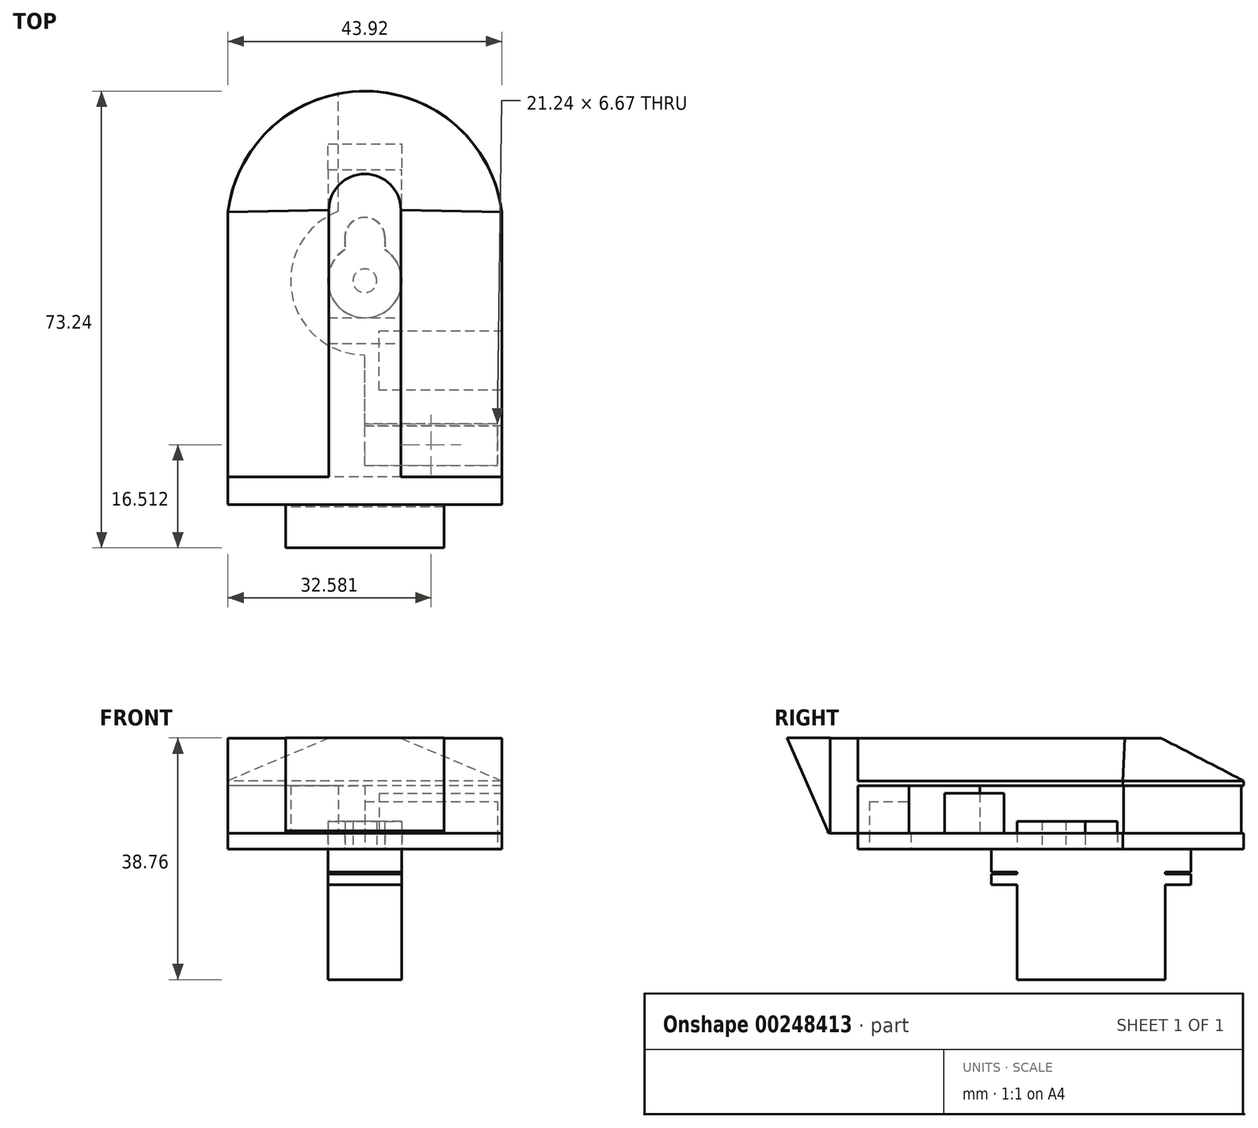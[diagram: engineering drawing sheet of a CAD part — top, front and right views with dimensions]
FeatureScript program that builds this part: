
annotation { "Feature Type Name" : "Feature", "Feature Type Description" : "" }
export const myFeature = defineFeature(function(context is Context, id is Id, definition is map)
    precondition{}
    {
        {
            var Q0;
            Q0=qCreatedBy(makeId("Top.planeOp"),FACE);
            var sketch = newSketch(context, id + "F0", { "sketchPlane" : qUnion([Q0])});
            skLineSegment(sketch, "E0", {"start": v(-5.9, 11.87) * mm, "end": v(-5.9, -11.87) * mm});
            skLineSegment(sketch, "E1", {"start": v(-5.9, -11.87) * mm, "end": v(5.9, -11.87) * mm});
            skLineSegment(sketch, "E2", {"start": v(5.9, -11.87) * mm, "end": v(5.9, 11.87) * mm});
            skLineSegment(sketch, "E3", {"start": v(5.9, 11.87) * mm, "end": v(-5.9, 11.87) * mm});
            skLineSegment(sketch, "E4", {"start": v(-5.9, 11.87) * mm, "end": v(-5.9, 16) * mm});
            skLineSegment(sketch, "E5", {"start": v(-5.9, 16) * mm, "end": v(5.9, 16) * mm});
            skLineSegment(sketch, "E6", {"start": v(5.9, 16) * mm, "end": v(5.9, 11.87) * mm});
            skLineSegment(sketch, "E7.MirrorCS", {"start": v(-5.9, -11.87) * mm, "end": v(-5.9, -16) * mm});
            skLineSegment(sketch, "E8.MirrorCS", {"start": v(-5.9, -16) * mm, "end": v(5.9, -16) * mm});
            skLineSegment(sketch, "E9.MirrorCS", {"start": v(5.9, -16) * mm, "end": v(5.9, -11.87) * mm});
            skSolve(sketch);
        }
        {
            var Q0;
            Q0=makeQuery(id+"F0.imprint","IMPRINT",FACE,{"disambiguationData":[TD([[makeQuery(id+"F0.imprint","IMPRINT",EDGE,{"derivedFrom":sQuery(id+"F0.wireOp",EDGE,"E0")}),1.0]])]});
            extrude(context, id + "F1", {"entities" : qUnion([Q0]), "oppositeDirection" : true, "depth" : 15.24 * mm});
        }
        {
            var Q0;
            Q0=makeQuery(id+"F0.imprint","IMPRINT",FACE,{"disambiguationData":[TD([[makeQuery(id+"F0.imprint","IMPRINT",EDGE,{"derivedFrom":sQuery(id+"F0.wireOp",EDGE,"E0")}),1.0]])]});
            extrude(context, id + "F2", {"entities" : qUnion([Q0]), "operationType" : NewBodyOperationType.ADD, "depth" : 5.7 * mm});
        }
        {
            var Q0;
            Q0=makeQuery(id+"F2.opExtrude","CAP_FACE",FACE,{"disambiguationData":[OSD([sQuery(id+"F0.wireOp",EDGE,"E0"),sQuery(id+"F0.wireOp",EDGE,"E1"),sQuery(id+"F0.wireOp",EDGE,"E2"),sQuery(id+"F0.wireOp",EDGE,"E3")])],"isStart":false});
            var sketch = newSketch(context, id + "F3", { "sketchPlane" : qUnion([Q0])});
            skArc(sketch, "E10", {"start": v(-3.17, -0.96) * mm, "mid": v(0, -11.85) * mm, "end": v(3.17, -0.96) * mm});
            skCircle(sketch, "E11", {"center": v(0, -5.94) * mm, "radius": 1.9 * mm});
            skArc(sketch, "E12", {"start": v(3.17, 1.02) * mm, "mid": v(0, 4.2) * mm, "end": v(-3.17, 1.02) * mm});
            skLineSegment(sketch, "E13", {"start": v(-3.17, 1.02) * mm, "end": v(-3.17, -0.96) * mm});
            skLineSegment(sketch, "E14", {"start": v(3.17, 1.02) * mm, "end": v(3.17, -0.96) * mm});
            skSolve(sketch);
        }
        {
            var Q0;
            Q0 = qSketchRegion(id + "F3", true);
            extrude(context, id + "F4", {"entities" : qUnion([Q0]), "operationType" : NewBodyOperationType.ADD, "depth" : 4.44 * mm});
        }
        {
            var Q0;
            Q0=makeQuery(id+"F0.imprint","IMPRINT",FACE,{"disambiguationData":[TD([[makeQuery(id+"F0.imprint","IMPRINT",EDGE,{"derivedFrom":sQuery(id+"F0.wireOp",EDGE,"E1")}),-1.0]])]});
            var Q1;
            Q1=makeQuery(id+"F0.imprint","IMPRINT",FACE,{"disambiguationData":[TD([[makeQuery(id+"F0.imprint","IMPRINT",EDGE,{"derivedFrom":sQuery(id+"F0.wireOp",EDGE,"E3")}),-1.0]])]});
            extrude(context, id + "F5", {"entities" : qUnion([Q0, Q1]), "operationType" : NewBodyOperationType.ADD, "depth" : 1.68 * mm});
        }
        {
            var Q0;
            Q0=qCreatedBy(makeId("Top.planeOp"),FACE);
            cPlane(context, id + "F6", {"entities" : qUnion([Q0]), "cplaneType" : CPlaneType.OFFSET, "offset" : 5.7 * mm, "width" : 152.4 * mm, "height" : 152.4 * mm});
        }
        {
            var Q0;
            Q0=qCreatedBy(id+"F6.planeOp",FACE);
            var sketch = newSketch(context, id + "F7", { "sketchPlane" : qUnion([Q0])});
            skLineSegment(sketch, "E15", {"start": v(21.96, -37.36) * mm, "end": v(-21.96, -37.36) * mm});
            skLineSegment(sketch, "E16", {"start": v(-21.96, -37.36) * mm, "end": v(-21.96, 5.1) * mm});
            skLineSegment(sketch, "E17", {"start": v(21.96, -37.36) * mm, "end": v(21.96, 5.1) * mm});
            skArc(sketch, "E18", {"start": v(21.96, 5.1) * mm, "mid": v(0, 24.49) * mm, "end": v(-21.96, 5.1) * mm});
            skArc(sketch, "E19", {"start": v(-3.23, -0.92) * mm, "mid": v(0, -11.87) * mm, "end": v(3.23, -0.92) * mm});
            skArc(sketch, "E20", {"start": v(3.23, 1.01) * mm, "mid": v(0, 4.25) * mm, "end": v(-3.23, 1.01) * mm});
            skLineSegment(sketch, "E21", {"start": v(-3.23, 1.01) * mm, "end": v(-3.23, -0.92) * mm});
            skLineSegment(sketch, "E22", {"start": v(3.23, 1.01) * mm, "end": v(3.23, -0.92) * mm});
            skSolve(sketch);
        }
        {
            var Q0;
            Q0 = qSketchRegion(id + "F7", true);
            extrude(context, id + "F8", {"entities" : qUnion([Q0]), "depth" : 2.54 * mm});
        }
        {
            var Q0;
            Q0=makeQuery(id+"F8.opExtrude","CAP_FACE",FACE,{"disambiguationData":[OSD([sQuery(id+"F7.wireOp",EDGE,"E15"),sQuery(id+"F7.wireOp",EDGE,"E16"),sQuery(id+"F7.wireOp",EDGE,"E17"),sQuery(id+"F7.wireOp",EDGE,"E18"),sQuery(id+"F7.wireOp",EDGE,"E19"),sQuery(id+"F7.wireOp",EDGE,"E20"),sQuery(id+"F7.wireOp",EDGE,"E21"),sQuery(id+"F7.wireOp",EDGE,"E22")])],"isStart":false});
            var sketch = newSketch(context, id + "F9", { "sketchPlane" : qUnion([Q0])});
            skLineSegment(sketch, "E23", {"start": v(21.96, -37.36) * mm, "end": v(-21.96, -37.36) * mm});
            skLineSegment(sketch, "E24", {"start": v(-21.96, -37.36) * mm, "end": v(-21.96, 5.1) * mm});
            skArc(sketch, "E25", {"start": v(-4.26, 24.07) * mm, "mid": v(-16.18, 17.45) * mm, "end": v(-21.96, 5.1) * mm});
            skArc(sketch, "E26", {"start": v(-4.26, 5.2) * mm, "mid": v(-11.7, -8.08) * mm, "end": v(0, -17.82) * mm});
            skLineSegment(sketch, "E27", {"start": v(-4.26, 5.2) * mm, "end": v(-4.26, 24.07) * mm});
            skLineSegment(sketch, "E28", {"start": v(2.29, -13.96) * mm, "end": v(21.97, -13.96) * mm});
            skLineSegment(sketch, "E29", {"start": v(21.97, -13.96) * mm, "end": v(21.97, -23.51) * mm});
            skLineSegment(sketch, "E30", {"start": v(2.29, -23.51) * mm, "end": v(2.29, -13.96) * mm});
            skLineSegment(sketch, "E31", {"start": v(21.96, -23.51) * mm, "end": v(2.29, -23.51) * mm});
            skLineSegment(sketch, "E32", {"start": v(21.96, -29.2) * mm, "end": v(21.96, -37.36) * mm});
            skLineSegment(sketch, "E33", {"start": v(21.96, -29.2) * mm, "end": v(0, -29.2) * mm});
            skLineSegment(sketch, "E34", {"start": v(0, -29.2) * mm, "end": v(0, -17.82) * mm});
            skSolve(sketch);
        }
        {
            var Q0;
            Q0=makeQuery(id+"F9.imprint","IMPRINT",FACE,{"disambiguationData":[TD([[makeQuery(id+"F9.imprint","IMPRINT",EDGE,{"derivedFrom":sQuery(id+"F9.wireOp",EDGE,"E23")}),-1.0]])]});
            extrude(context, id + "F10", {"entities" : qUnion([Q0]), "depth" : 7.62 * mm});
        }
        {
            var Q0;
            Q0=makeQuery(id+"F9.imprint","IMPRINT",FACE,{"disambiguationData":[TD([[makeQuery(id+"F9.imprint","IMPRINT",EDGE,{"derivedFrom":sQuery(id+"F9.wireOp",EDGE,"E28")}),-1.0]])]});
            var Q1;
            {var subQ0=sQuery(id+"F9.wireOp",EDGE,"E30");Q1=makeQuery(id+"F9.imprint","IMPRINT",FACE,{"disambiguationData":[TD([[makeQuery(id+"F9.imprint","IMPRINT",EDGE,{"derivedFrom":subQ0}),-1.0]])]});}
            extrude(context, id + "F11", {"entities" : qUnion([Q0, Q1]), "depth" : 6.4 * mm});
        }
        {
            var Q0;
            Q0=makeQuery(id+"F8.opExtrude","CAP_FACE",FACE,{"disambiguationData":[OSD([sQuery(id+"F7.wireOp",EDGE,"E15"),sQuery(id+"F7.wireOp",EDGE,"E16"),sQuery(id+"F7.wireOp",EDGE,"E17"),sQuery(id+"F7.wireOp",EDGE,"E18"),sQuery(id+"F7.wireOp",EDGE,"E19"),sQuery(id+"F7.wireOp",EDGE,"E20"),sQuery(id+"F7.wireOp",EDGE,"E21"),sQuery(id+"F7.wireOp",EDGE,"E22")])],"isStart":true});
            var sketch = newSketch(context, id + "F12", { "sketchPlane" : qUnion([Q0])});
            skLineSegment(sketch, "E35", {"start": v(21.24, 35.57) * mm, "end": v(0, 35.57) * mm});
            skLineSegment(sketch, "E36", {"start": v(0, 35.57) * mm, "end": v(0, 28.9) * mm});
            skLineSegment(sketch, "E37", {"start": v(21.24, 35.57) * mm, "end": v(21.24, 28.9) * mm});
            skLineSegment(sketch, "E38", {"start": v(21.24, 28.9) * mm, "end": v(0, 28.9) * mm});
            skSolve(sketch);
        }
        {
            var Q0;
            Q0=makeQuery(id+"F12.imprint","IMPRINT",FACE,{"disambiguationData":[TD([[makeQuery(id+"F12.imprint","IMPRINT",EDGE,{"derivedFrom":sQuery(id+"F12.wireOp",EDGE,"E35")}),1.0]])]});
            extrude(context, id + "F13", {"entities" : qUnion([Q0]), "operationType" : NewBodyOperationType.REMOVE, "oppositeDirection" : true, "depth" : 7.62 * mm});
        }
        {
            var Q0;
            Q0=makeQuery(id+"F8.opExtrude","CAP_FACE",FACE,{"disambiguationData":[OSD([sQuery(id+"F7.wireOp",EDGE,"E15"),sQuery(id+"F7.wireOp",EDGE,"E16"),sQuery(id+"F7.wireOp",EDGE,"E17"),sQuery(id+"F7.wireOp",EDGE,"E18"),sQuery(id+"F7.wireOp",EDGE,"E19"),sQuery(id+"F7.wireOp",EDGE,"E20"),sQuery(id+"F7.wireOp",EDGE,"E21"),sQuery(id+"F7.wireOp",EDGE,"E22")])],"isStart":true});
            var sketch = newSketch(context, id + "F14", { "sketchPlane" : qUnion([Q0])});
            skLineSegment(sketch, "E39", {"start": v(-5.9, -11.87) * mm, "end": v(5.9, -11.87) * mm});
            skLineSegment(sketch, "E40", {"start": v(5.9, 11.87) * mm, "end": v(-5.9, 11.87) * mm});
            skLineSegment(sketch, "E41", {"start": v(-5.9, 11.87) * mm, "end": v(-5.9, 16) * mm});
            skLineSegment(sketch, "E42", {"start": v(-5.9, 16) * mm, "end": v(5.9, 16) * mm});
            skLineSegment(sketch, "E43", {"start": v(5.9, 16) * mm, "end": v(5.9, 11.87) * mm});
            skLineSegment(sketch, "E44.MirrorCS", {"start": v(-5.9, -11.87) * mm, "end": v(-5.9, -16) * mm});
            skLineSegment(sketch, "E45.MirrorCS", {"start": v(-5.9, -16) * mm, "end": v(5.9, -16) * mm});
            skLineSegment(sketch, "E46.MirrorCS", {"start": v(5.9, -16) * mm, "end": v(5.9, -11.87) * mm});
            skSolve(sketch);
        }
        {
            var Q0;
            Q0 = qSketchRegion(id + "F14", true);
            extrude(context, id + "F15", {"entities" : qUnion([Q0]), "operationType" : NewBodyOperationType.ADD, "depth" : 3.7 * mm});
        }
        {
            var Q0;
            Q0=makeQuery(id+"F10.opExtrude","CAP_FACE",FACE,{"disambiguationData":[OSD([sQuery(id+"F9.wireOp",EDGE,"E23"),sQuery(id+"F9.wireOp",EDGE,"E24"),sQuery(id+"F9.wireOp",EDGE,"E25"),sQuery(id+"F9.wireOp",EDGE,"E26"),sQuery(id+"F9.wireOp",EDGE,"E27"),sQuery(id+"F9.wireOp",EDGE,"E32"),sQuery(id+"F9.wireOp",EDGE,"E33"),sQuery(id+"F9.wireOp",EDGE,"E34")])],"isStart":false});
            var sketch = newSketch(context, id + "F16", { "sketchPlane" : qUnion([Q0])});
            skLineSegment(sketch, "E47", {"start": v(21.96, -42.14) * mm, "end": v(-21.96, -42.14) * mm});
            skLineSegment(sketch, "E48", {"start": v(-21.96, -37.36) * mm, "end": v(-21.96, 5.1) * mm});
            skLineSegment(sketch, "E49", {"start": v(21.96, -37.36) * mm, "end": v(21.96, 5.1) * mm});
            skArc(sketch, "E50", {"start": v(21.96, 5.1) * mm, "mid": v(0, 24.49) * mm, "end": v(-21.96, 5.1) * mm});
            skLineSegment(sketch, "E51", {"start": v(-21.96, -37.36) * mm, "end": v(21.96, -37.36) * mm});
            skLineSegment(sketch, "E52", {"start": v(-21.96, -37.36) * mm, "end": v(-21.96, -42.14) * mm});
            skLineSegment(sketch, "E53", {"start": v(21.96, -37.36) * mm, "end": v(21.96, -42.14) * mm});
            skSolve(sketch);
        }
        {
            var Q0;
            Q0=makeQuery(id+"F16.imprint","IMPRINT",FACE,{"disambiguationData":[TD([[makeQuery(id+"F16.imprint","IMPRINT",EDGE,{"derivedFrom":sQuery(id+"F16.wireOp",EDGE,"E47")}),-1.0]])]});
            var Q1;
            {var subQ2=sQuery(id+"F16.wireOp",EDGE,"C74SLhbN-AlEZ-A5yF-sOJ7-cix4Ruc3rFjT");Q1=makeQuery(id+"F16.imprint","IMPRINT",FACE,{"disambiguationData":[TD([[makeQuery(id+"F16.imprint","IMPRINT",EDGE,{"derivedFrom":subQ2}),1.0]])]});}
            extrude(context, id + "F17", {"entities" : qUnion([Q0, Q1]), "depth" : 15.24 * mm, "offsetDistance" : 25.4 * mm, "symmetric" : true});
        }
        {
            var Q0;
            Q0=qCreatedBy(makeId("Right.planeOp"),FACE);
            var sketch = newSketch(context, id + "F18", { "sketchPlane" : qUnion([Q0])});
            skLineSegment(sketch, "E54", {"start": v(-41.86, 23.52) * mm, "end": v(-48.75, 23.52) * mm});
            skLineSegment(sketch, "E55", {"start": v(-41.86, 8.26) * mm, "end": v(-42.2, 8.26) * mm});
            skLineSegment(sketch, "E56", {"start": v(-42.2, 8.26) * mm, "end": v(-42.2, 8.62) * mm});
            skLineSegment(sketch, "E57", {"start": v(-41.86, 23.52) * mm, "end": v(-41.86, 8.26) * mm});
            skLineSegment(sketch, "E58", {"start": v(-48.75, 23.52) * mm, "end": v(-42.2, 8.62) * mm});
            skSolve(sketch);
        }
        {
            var Q0;
            {var subQ0=sQuery(id+"F18.wireOp",EDGE,"E55");Q0=makeQuery(id+"F18.imprint","IMPRINT",FACE,{"disambiguationData":[TD([[makeQuery(id+"F18.imprint","IMPRINT",EDGE,{"derivedFrom":subQ0}),-1.0]])]});}
            extrude(context, id + "F19", {"entities" : qUnion([Q0]), "operationType" : NewBodyOperationType.REMOVE, "oppositeDirection" : true, "depth" : 50.8 * mm, "offsetDistance" : 25.4 * mm, "symmetric" : true});
        }
        {
            var Q0;
            Q0=makeQuery(id+"F10.opExtrude","CAP_FACE",FACE,{"disambiguationData":[OSD([sQuery(id+"F9.wireOp",EDGE,"E23"),sQuery(id+"F9.wireOp",EDGE,"E24"),sQuery(id+"F9.wireOp",EDGE,"E25"),sQuery(id+"F9.wireOp",EDGE,"E26"),sQuery(id+"F9.wireOp",EDGE,"E27"),sQuery(id+"F9.wireOp",EDGE,"E32"),sQuery(id+"F9.wireOp",EDGE,"E33"),sQuery(id+"F9.wireOp",EDGE,"E34")])],"isStart":false});
            var Q1;
            Q1=makeQuery(id+"F16.imprint","IMPRINT",FACE,{"disambiguationData":[TD([[makeQuery(id+"F16.imprint","IMPRINT",EDGE,{"derivedFrom":makeQuery(id+"F10.opExtrude","CAP_EDGE",EDGE,{"disambiguationData":[OSD([sQuery(id+"F9.wireOp",EDGE,"E26")])],"isStart":false})}),1.0]])]});
            extrude(context, id + "F20", {"entities" : qUnion([Q0, Q1]), "depth" : 0.76 * mm});
        }
        {
            var Q0;
            Q0=makeQuery(id+"F20.opExtrude","SWEPT_BODY",BODY,{"disambiguationData":[OSD([sQuery(id+"F9.wireOp",EDGE,"E26"),sQuery(id+"F9.wireOp",EDGE,"E27"),sQuery(id+"F9.wireOp",EDGE,"E33"),sQuery(id+"F9.wireOp",EDGE,"E34"),sQuery(id+"F16.wireOp",EDGE,"E49"),sQuery(id+"F16.wireOp",EDGE,"E50")])]});
            var Q1;
            Q1=makeQuery(id+"F20.opExtrude","SWEPT_BODY",BODY,{"disambiguationData":[OSD([sQuery(id+"F9.wireOp",EDGE,"E23"),sQuery(id+"F9.wireOp",EDGE,"E24"),sQuery(id+"F9.wireOp",EDGE,"E25"),sQuery(id+"F9.wireOp",EDGE,"E26"),sQuery(id+"F9.wireOp",EDGE,"E27"),sQuery(id+"F9.wireOp",EDGE,"E32"),sQuery(id+"F9.wireOp",EDGE,"E33"),sQuery(id+"F9.wireOp",EDGE,"E34")])]});
            booleanBodies(context, id + "F21", {"operationType" : BooleanOperationType.UNION, "tools" : qUnion([Q0, Q1])});
        }
        {
            var Q0;
            Q0=makeQuery(id+"F17.opExtrude","CAP_FACE",FACE,{"disambiguationData":[OSD([sQuery(id+"F16.wireOp",EDGE,"E47"),sQuery(id+"F16.wireOp",EDGE,"f3ImOjVg-Zw3k-SrhR-BsUI-0FnWvnqxl6u0"),sQuery(id+"F16.wireOp",EDGE,"C74SLhbN-AlEZ-A5yF-sOJ7-cix4Ruc3rFjT"),sQuery(id+"F16.wireOp",EDGE,"eIBPg6GD-pLcm-TFRZ-aouF-WUSqO2R7U4Q8")])],"isStart":false});
            var sketch = newSketch(context, id + "F22", { "sketchPlane" : qUnion([Q0])});
            skLineSegment(sketch, "E59", {"start": v(-5.76, -37.36) * mm, "end": v(5.76, -37.36) * mm});
            skArc(sketch, "E60", {"start": v(5.76, 5.43) * mm, "mid": v(0, 11.2) * mm, "end": v(-5.76, 5.43) * mm});
            skLineSegment(sketch, "E61", {"start": v(-5.76, 5.43) * mm, "end": v(-5.76, -37.36) * mm});
            skLineSegment(sketch, "E62", {"start": v(5.76, 5.43) * mm, "end": v(5.76, -37.36) * mm});
            skSolve(sketch);
        }
        {
            var Q1;
            Q1=makeQuery(id+"F22.imprint","IMPRINT",FACE,{"disambiguationData":[TD([[makeQuery(id+"F22.imprint","IMPRINT",EDGE,{"derivedFrom":sQuery(id+"F22.wireOp",EDGE,"E59")}),-1.0]])]});
            var Q2;
            {var subQ0=sQuery(id+"F9.wireOp",EDGE,"E34");var subQ1=sQuery(id+"F9.wireOp",EDGE,"E33");var subQ2=sQuery(id+"F9.wireOp",EDGE,"E27");var subQ3=sQuery(id+"F9.wireOp",EDGE,"E26");Q2=makeQuery(id+"F21.opBoolean","MERGE",FACE,{"derivedFrom":[makeQuery(id+"F20.opExtrude","CAP_FACE",FACE,{"disambiguationData":[OSD([sQuery(id+"F9.wireOp",EDGE,"E23"),sQuery(id+"F9.wireOp",EDGE,"E24"),sQuery(id+"F9.wireOp",EDGE,"E25"),subQ3,subQ2,sQuery(id+"F9.wireOp",EDGE,"E32"),subQ1,subQ0])],"isStart":false}),makeQuery(id+"F20.opExtrude","CAP_FACE",FACE,{"disambiguationData":[OSD([subQ3,subQ2,subQ1,subQ0,sQuery(id+"F16.wireOp",EDGE,"E49"),sQuery(id+"F16.wireOp",EDGE,"E50")])],"isStart":false})]});}
            loft(context, id + "F23", {"operationType" : NewBodyOperationType.ADD, "sheetProfilesArray" : [{ "sheetProfileEntities" : qUnion([Q1]) }, { "sheetProfileEntities" : qUnion([Q2]) }]});
        }
        {
            var Q0;
            Q0=makeQuery(id+"F18.imprint","IMPRINT",FACE,{"disambiguationData":[TD([[makeQuery(id+"F18.imprint","IMPRINT",EDGE,{"derivedFrom":sQuery(id+"F18.wireOp",EDGE,"E54")}),1.0]])]});
            extrude(context, id + "F24", {"entities" : qUnion([Q0]), "operationType" : NewBodyOperationType.ADD, "depth" : 25.4 * mm, "offsetDistance" : 25.4 * mm, "symmetric" : true});
        }
    });
